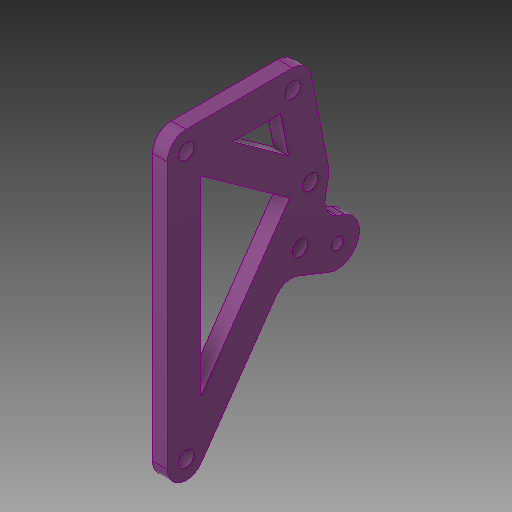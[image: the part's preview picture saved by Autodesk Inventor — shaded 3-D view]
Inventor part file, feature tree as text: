
AUTODESK INVENTOR PART (.ipt)
format: ipt  version: 2017 SP1 (Build 210196100, 196)  size: 176,640 bytes
history: native  units: in
note: dims shown in document units (in); Inventor stores cm internally (conversion verified against a paired STEP export)
features: extrude x2, sketch x2, projected_geometry x1
ambient origin geometry x8: Origin, YZ Plane, XZ Plane, XY Plane, X Axis, Y Axis, Z Axis, Center Point
bodies: Solid1 (feature_tree)
feature tree (5):
  extrude  "Extrusion1"  Depth=0.26in
  extrude  "Extrusion2"  Depth=0.25in
  sketch  "Sketch1"  dims[d0=1.0in d1=0.26in]
  sketch  "Sketch5"  dims[d2=0.548in d3=1.25in d4=1.5in d5=3.0in d7=0.25in d8=0.0in d10=1.0in d14=0.25in d48=0.25in d57=0.1875in d58=0.0in d59=0.1875in d62=0.875in d63=0.875in d65=1.125in d66=1.5in d67=0.2in d68=0.25in]
  projected_geometry  "Projected Loop1"
